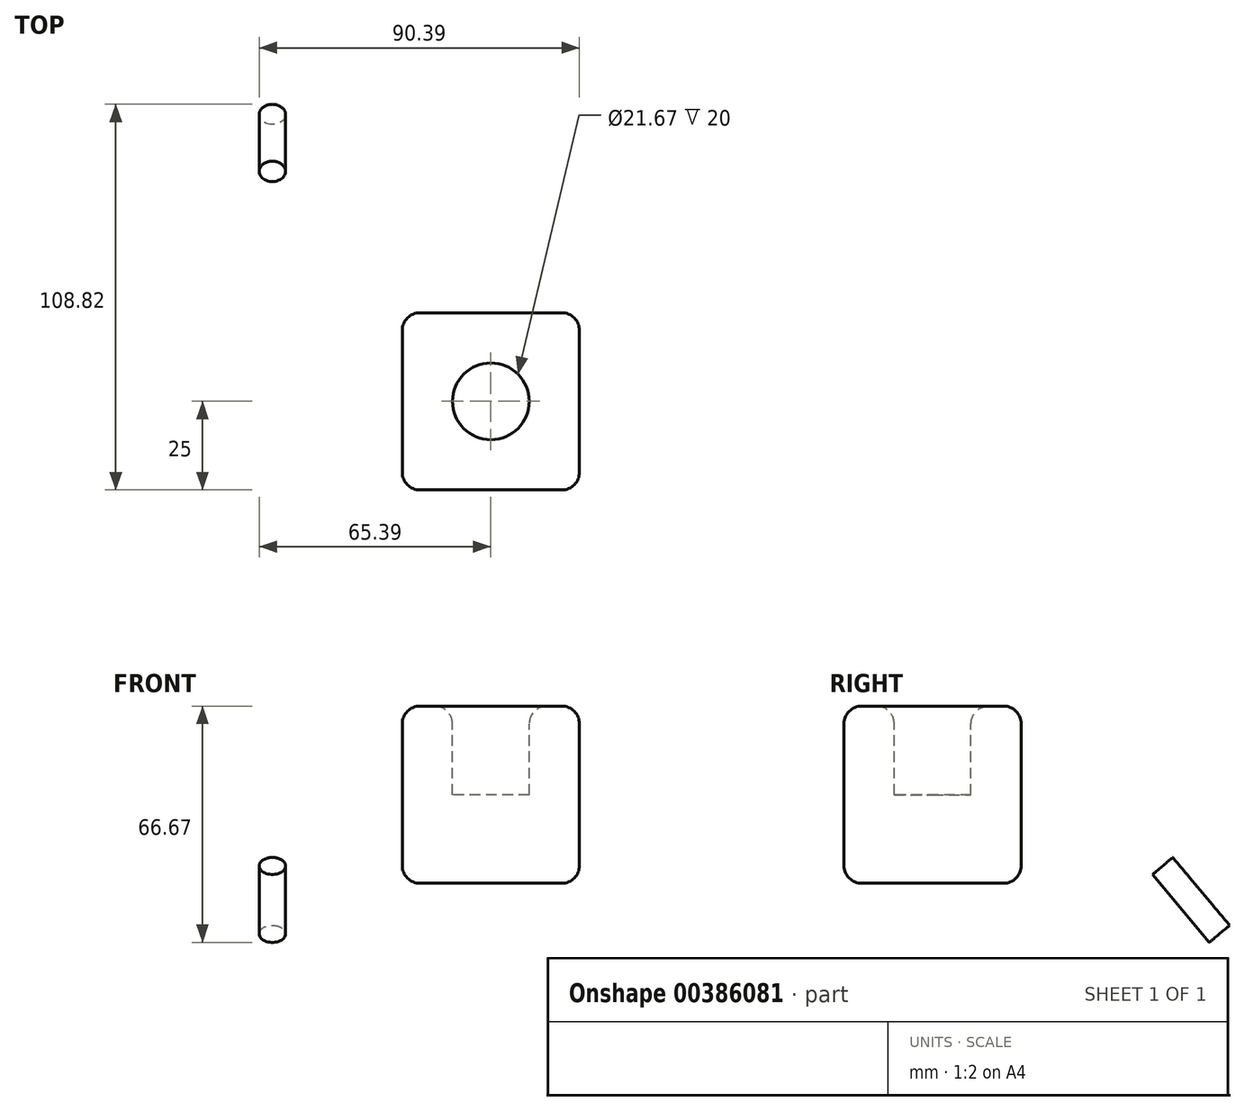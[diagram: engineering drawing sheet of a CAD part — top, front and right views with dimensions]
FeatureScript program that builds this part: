
annotation { "Feature Type Name" : "Feature", "Feature Type Description" : "" }
export const myFeature = defineFeature(function(context is Context, id is Id, definition is map)
    precondition{}
    {
        {
            var Q0;
            Q0=qCreatedBy(makeId("Top.planeOp"),FACE);
            var sketch = newSketch(context, id + "F0", { "sketchPlane" : qUnion([Q0])});
            skLineSegment(sketch, "E0.bottom", {"start": v(25, -25) * mm, "end": v(-25, -25) * mm});
            skLineSegment(sketch, "E0.top", {"start": v(25, 25) * mm, "end": v(-25, 25) * mm});
            skLineSegment(sketch, "E0.left", {"start": v(25, -25) * mm, "end": v(25, 25) * mm});
            skLineSegment(sketch, "E0.right", {"start": v(-25, -25) * mm, "end": v(-25, 25) * mm});
            skPoint(sketch, "E0.middle", {"position": v(0, 0) * mm});
            skSolve(sketch);
        }
        {
            var Q0;
            Q0=makeQuery(id+"F0.imprint","IMPRINT",FACE,{"disambiguationData":[TD([[makeQuery(id+"F0.imprint","IMPRINT",EDGE,{"derivedFrom":sQuery(id+"F0.wireOp",EDGE,"E0.bottom")}),-1.0]])]});
            extrude(context, id + "F1", {"entities" : qUnion([Q0]), "depth" : 50 * mm});
        }
        {
            var Q0;
            Q0=makeQuery(id+"F1.opExtrude","CAP_FACE",FACE,{"disambiguationData":[OSD([sQuery(id+"F0.wireOp",EDGE,"E0.bottom"),sQuery(id+"F0.wireOp",EDGE,"E0.top"),sQuery(id+"F0.wireOp",EDGE,"E0.left"),sQuery(id+"F0.wireOp",EDGE,"E0.right")])],"isStart":false});
            var sketch = newSketch(context, id + "F2", { "sketchPlane" : qUnion([Q0])});
            skCircle(sketch, "E1", {"center": v(0, 0) * mm, "radius": 10.84 * mm});
            skSolve(sketch);
        }
        {
            var Q0;
            Q0=makeQuery(id+"F2.imprint","IMPRINT",FACE,{"disambiguationData":[TD([[makeQuery(id+"F2.imprint","IMPRINT",EDGE,{"derivedFrom":sQuery(id+"F2.wireOp",EDGE,"E1")}),1.0]])]});
            extrude(context, id + "F3", {"entities" : qUnion([Q0]), "operationType" : NewBodyOperationType.REMOVE, "oppositeDirection" : true, "depth" : 25 * mm});
        }
        {
            var Q0;
            Q0=makeQuery(id+"F1.opExtrude","CAP_EDGE",EDGE,{"disambiguationData":[OSD([sQuery(id+"F0.wireOp",EDGE,"E0.right")])],"isStart":false});
            var Q1;
            Q1=makeQuery(id+"F1.opExtrude","CAP_FACE",FACE,{"disambiguationData":[OSD([sQuery(id+"F0.wireOp",EDGE,"E0.bottom"),sQuery(id+"F0.wireOp",EDGE,"E0.top"),sQuery(id+"F0.wireOp",EDGE,"E0.left"),sQuery(id+"F0.wireOp",EDGE,"E0.right")])],"isStart":false});
            fillet(context, id + "F4", {"entities" : qUnion([Q0, Q1]), "radius" : 5 * mm, "tangentPropagation" : true, "allowEdgeOverflow" : false});
        }
        {
            var Q0;
            Q0=makeQuery(id+"F4.opFillet","BLEND_EDGE",EDGE,{"blendedFrom":[makeQuery(id+"F1.opExtrude","CAP_EDGE",EDGE,{"disambiguationData":[OSD([sQuery(id+"F0.wireOp",EDGE,"E0.bottom")])],"isStart":false}),makeQuery(id+"F1.opExtrude","CAP_EDGE",EDGE,{"disambiguationData":[OSD([sQuery(id+"F0.wireOp",EDGE,"E0.right")])],"isStart":false})],"blendedInto":[]});
            var Q1;
            Q1=makeQuery(id+"F1.opExtrude","CAP_FACE",FACE,{"disambiguationData":[OSD([sQuery(id+"F0.wireOp",EDGE,"E0.bottom"),sQuery(id+"F0.wireOp",EDGE,"E0.top"),sQuery(id+"F0.wireOp",EDGE,"E0.left"),sQuery(id+"F0.wireOp",EDGE,"E0.right")])],"isStart":true});
            fillet(context, id + "F5", {"entities" : qUnion([Q0, Q1]), "radius" : 5 * mm, "tangentPropagation" : true, "allowEdgeOverflow" : false});
        }
        {
            var Q0;
            Q0=makeQuery(id+"F5.opFillet","BLEND_EDGE",EDGE,{"blendedFrom":[makeQuery(id+"F1.opExtrude","CAP_EDGE",EDGE,{"disambiguationData":[OSD([sQuery(id+"F0.wireOp",EDGE,"E0.bottom")])],"isStart":true}),makeQuery(id+"F1.opExtrude","CAP_EDGE",EDGE,{"disambiguationData":[OSD([sQuery(id+"F0.wireOp",EDGE,"E0.left")])],"isStart":true})],"blendedInto":[]});
            var Q1;
            {var subQ0=sQuery(id+"F0.wireOp",EDGE,"E0.left");Q1=makeQuery(id+"F5.opFillet","BLEND_EDGE",EDGE,{"blendedFrom":[makeQuery(id+"F1.opExtrude","CAP_EDGE",EDGE,{"disambiguationData":[OSD([subQ0])],"isStart":true}),makeQuery(id+"F1.opExtrude","SWEPT_FACE",FACE,{"disambiguationData":[OSD([subQ0])]})],"blendedInto":[makeQuery(id+"F1.opExtrude","SWEPT_FACE",FACE,{"disambiguationData":[OSD([subQ0])]})]});}
            fillet(context, id + "F6", {"entities" : qUnion([Q0, Q1]), "radius" : 5 * mm, "tangentPropagation" : true, "allowEdgeOverflow" : false});
        }
        {
            var Q0;
            Q0=makeQuery(id+"F5.opFillet","BLEND_FACE",FACE,{"disambiguationData":[OSD([sQuery(id+"F0.wireOp",EDGE,"E0.top")])]});
            fillet(context, id + "F7", {"entities" : qUnion([Q0]), "radius" : 5 * mm, "tangentPropagation" : true, "allowEdgeOverflow" : false});
        }
        {
            var Q0;
            Q0=qCreatedBy(makeId("Top.planeOp"),FACE);
            var sketch = newSketch(context, id + "F8", { "sketchPlane" : qUnion([Q0])});
            skLineSegment(sketch, "E2.bottom", {"start": v(-48.53, 59.09) * mm, "end": v(-76.68, 59.09) * mm});
            skLineSegment(sketch, "E2.top", {"start": v(-48.53, 77.49) * mm, "end": v(-76.68, 77.49) * mm});
            skLineSegment(sketch, "E2.left", {"start": v(-48.53, 59.09) * mm, "end": v(-48.53, 77.49) * mm});
            skLineSegment(sketch, "E2.right", {"start": v(-76.68, 59.09) * mm, "end": v(-76.68, 77.49) * mm});
            skPoint(sketch, "E2.middle", {"position": v(-62.6, 68.29) * mm});
            skLineSegment(sketch, "E3", {"start": v(-24, 52.23) * mm, "end": v(-24, 30.4) * mm});
            skSolve(sketch);
        }
        {
            var Q0;
            Q0=sQuery(id+"F8.wireOp",EDGE,"E2.bottom");
            var Q1;
            Q1=qCreatedBy(makeId("Top.planeOp"),FACE);
            cPlane(context, id + "F9", {"entities" : qUnion([Q0, Q1]), "cplaneType" : CPlaneType.LINE_ANGLE, "offset" : 25 * mm, "angle" : 40 * degree, "oppositeDirection" : true, "width" : 150 * mm, "height" : 150 * mm});
        }
        {
            var Q0;
            Q0=qCreatedBy(id+"F9.planeOp",FACE);
            var sketch = newSketch(context, id + "F10", { "sketchPlane" : qUnion([Q0])});
            skCircle(sketch, "E4", {"center": v(-61.66, -52.84) * mm, "radius": 3.73 * mm});
            skSolve(sketch);
        }
        {
            var Q0;
            Q0=makeQuery(id+"F10.imprint","IMPRINT",FACE,{"disambiguationData":[TD([[makeQuery(id+"F10.imprint","IMPRINT",EDGE,{"derivedFrom":sQuery(id+"F10.wireOp",EDGE,"E4")}),1.0]])]});
            extrude(context, id + "F11", {"entities" : qUnion([Q0]), "depth" : 25 * mm});
        }
    });
